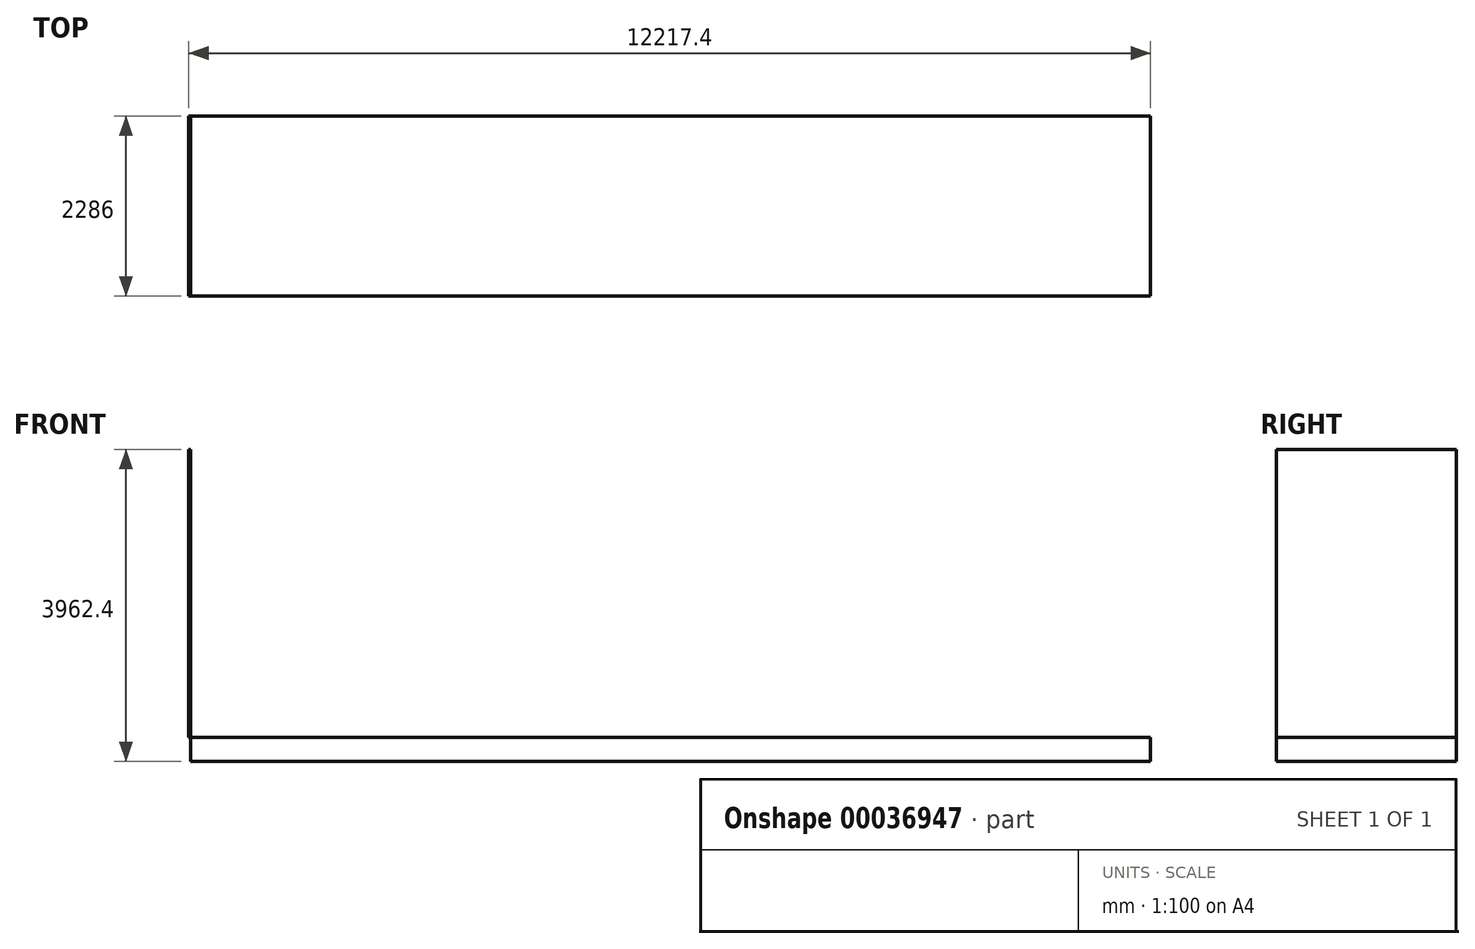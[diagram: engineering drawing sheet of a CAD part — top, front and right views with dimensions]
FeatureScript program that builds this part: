
annotation { "Feature Type Name" : "Feature", "Feature Type Description" : "" }
export const myFeature = defineFeature(function(context is Context, id is Id, definition is map)
    precondition{}
    {
        {
            var Q0;
            Q0=qCreatedBy(makeId("Top.planeOp"),FACE);
            var sketch = newSketch(context, id + "F0", { "sketchPlane" : qUnion([Q0])});
            skLineSegment(sketch, "E0.bottom", {"start": v(0, 0) * mm, "end": v(12192, 0) * mm});
            skLineSegment(sketch, "E0.top", {"start": v(0, 2286) * mm, "end": v(12192, 2286) * mm});
            skLineSegment(sketch, "E0.left", {"start": v(0, 0) * mm, "end": v(0, 2286) * mm});
            skLineSegment(sketch, "E0.right", {"start": v(12192, 0) * mm, "end": v(12192, 2286) * mm});
            skSolve(sketch);
        }
        {
            var Q0;
            Q0 = qSketchRegion(id + "F0", true);
            extrude(context, id + "F1", {"entities" : qUnion([Q0]), "oppositeDirection" : true, "depth" : 304.8 * mm});
        }
        {
            var Q0;
            Q0=makeQuery(id+"F1.opExtrude","SWEPT_FACE",FACE,{"disambiguationData":[OSD([sQuery(id+"F0.wireOp",EDGE,"E0.left")])]});
            var sketch = newSketch(context, id + "F2", { "sketchPlane" : qUnion([Q0])});
            skLineSegment(sketch, "E1.bottom", {"start": v(-2286, 0) * mm, "end": v(0, 0) * mm});
            skLineSegment(sketch, "E1.top", {"start": v(-2286, 3657.6) * mm, "end": v(0, 3657.6) * mm});
            skLineSegment(sketch, "E1.left", {"start": v(-2286, 0) * mm, "end": v(-2286, 3657.6) * mm});
            skLineSegment(sketch, "E1.right", {"start": v(0, 0) * mm, "end": v(0, 3657.6) * mm});
            skSolve(sketch);
        }
        {
            var Q0;
            Q0=makeQuery(id+"F2.imprint","IMPRINT",FACE,{"disambiguationData":[TD([[makeQuery(id+"F2.imprint","IMPRINT",EDGE,{"derivedFrom":sQuery(id+"F2.wireOp",EDGE,"E1.bottom")}),-1.0]])]});
            extrude(context, id + "F3", {"entities" : qUnion([Q0]), "depth" : 25.4 * mm});
        }
    });
